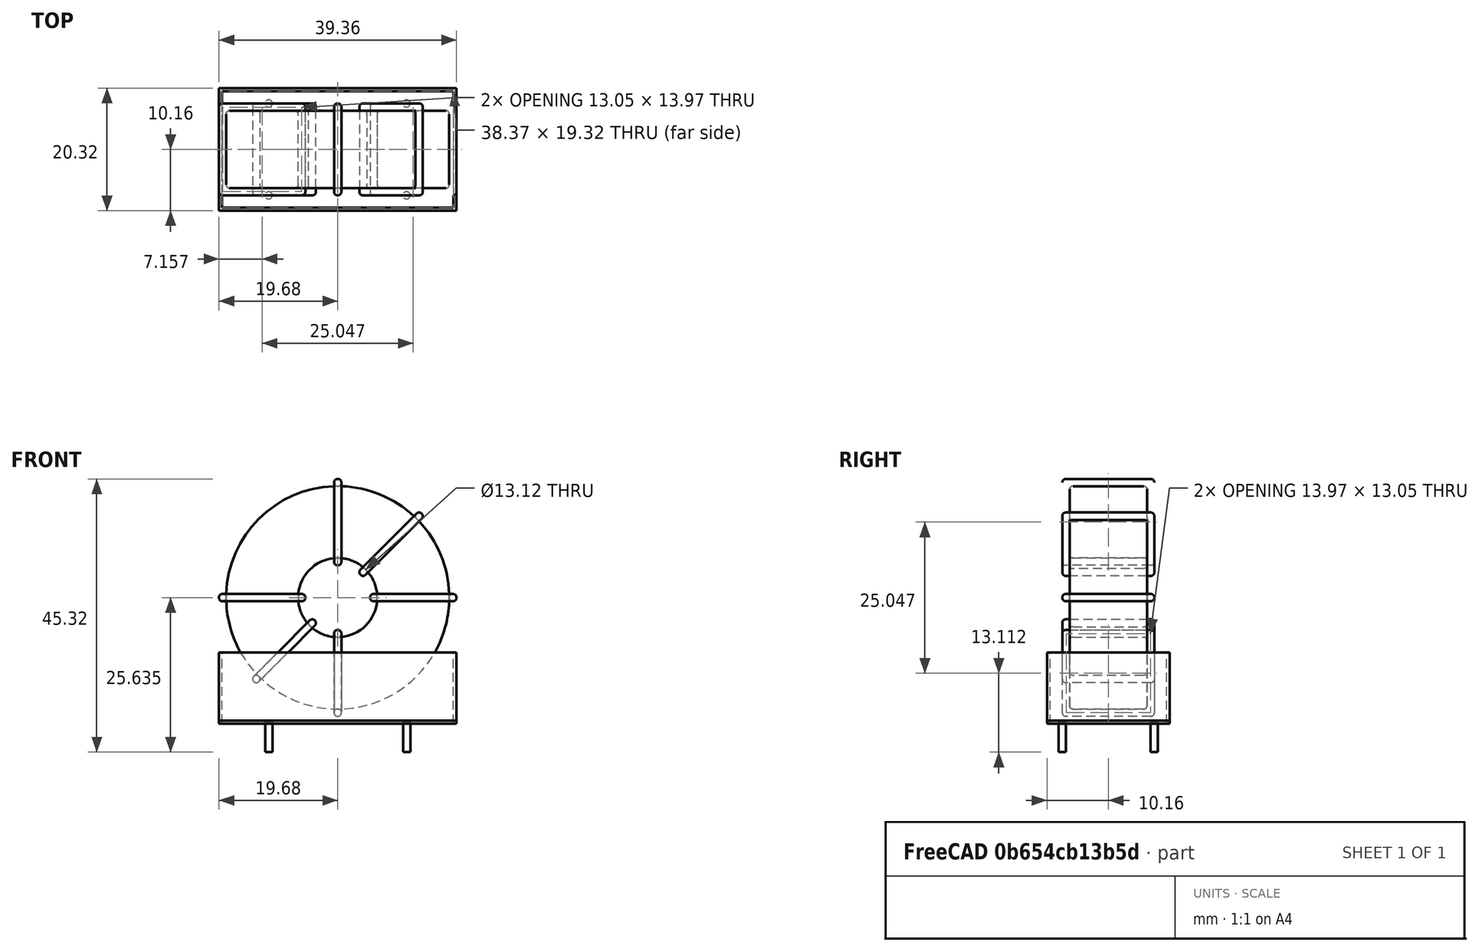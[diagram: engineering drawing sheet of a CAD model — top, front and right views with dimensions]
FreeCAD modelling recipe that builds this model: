
FCSTD DOCUMENT  (FreeCAD 0.16R6703 (Git))
Label: L_CommonModeChoke_Toroid_Vertical_L39.4mm_W20.3mm_Px15.24mm_Py22.86mm_Bourns_8100series
License: All rights reserved
LicenseURL: http://en.wikipedia.org/wiki/All_rights_reserved
objects: Sketcher::SketchObject×8, PartDesign::Pad×8, PartDesign::Fillet×5, Spreadsheet::Sheet×1
note: 29 computed .brp shape members not serialized (recipe doc carries the construction recipe); baked Part::Feature solids carry a one-line shape summary decoded from their .brp

FEATURE [Spreadsheet::Sheet] Spreadsheet  label="dimensions"
  cells = A1=Wx; B1(Wx)=39.37; C1(WW)=13.12333333333333; D1(iWx)=39.37; A2=Wy; B2(Wy)=15.24; D2(iWy)=20.32; A3=RM; B3(RMx)=15.24; C3(RMy)=22.86; A4=d_wire; B4(d_wire)=1.2; A5=H; B5(H)=31; A6=offsetx; B6(offsetx)=8.254999999999999
FEATURE [Sketcher::SketchObject] Sketch
  Placement = pos=(11.43,-7.62,0) rot=(1,0,0;1.5708rad)
  expr: Placement.Base.x = Spreadsheet.RMy / 2
  expr: Constraints[4] = Spreadsheet.WW / 2
  expr: Placement.Base.y = -Spreadsheet.RMx / 2
  expr: Constraints[0] = Spreadsheet.Wx / 2 - Spreadsheet.d_wire
  expr: Constraints[2] = Spreadsheet.Wx / 2 + Spreadsheet.d_wire + 0.5
  sketch-geometry (2):
    g0: Circle CenterX=0 CenterY=21.385 CenterZ=0 NormalX=0 NormalY=0 NormalZ=1 Radius=18.485
    g1: Circle CenterX=0 CenterY=21.385 CenterZ=0 NormalX=0 NormalY=0 NormalZ=1 Radius=6.56167
  constraints (5):
    c: Radius(g0) = 18.485
    c: DistanceX(g-1,g0) = 0
    c: DistanceY(g-1,g0) = 21.385
    c: Coincident(g1,g0)
    c: Radius(g1) = 6.56167
FEATURE [PartDesign::Pad] Pad
  Length = 12.84
  Length2 = 100
  Midplane = true
  Placement = pos=(11.43,-7.62,0) rot=(1,0,0;1.5708rad)
  Sketch = -> Sketch
  Type = 0
  expr: Length = Spreadsheet.Wy - 2 * Spreadsheet.d_wire
FEATURE [Sketcher::SketchObject] Sketch001
  Placement = pos=(0,0,0.75) rot=(0,0,1;0rad)
  expr: Constraints[4] = Spreadsheet.RMy
  expr: Constraints[2] = -Spreadsheet.RMx
  expr: Constraints[1] = Spreadsheet.d_wire / 2
  sketch-geometry (4):
    g0: Circle CenterX=0 CenterY=0 CenterZ=0 NormalX=0 NormalY=0 NormalZ=1 Radius=0.6
    g1: Circle CenterX=22.86 CenterY=-15.24 CenterZ=0 NormalX=0 NormalY=0 NormalZ=1 Radius=0.6
    g2: Circle CenterX=0 CenterY=-15.24 CenterZ=0 NormalX=0 NormalY=0 NormalZ=1 Radius=0.6
    g3: Circle CenterX=22.86 CenterY=0 CenterZ=0 NormalX=0 NormalY=0 NormalZ=1 Radius=0.6
  constraints (11):
    c: Equal(g0,g1)
    c: Radius(g0) = 0.6
    c: DistanceY(g-1,g1) = -15.24
    c: Coincident(g0,g-1)
    c: DistanceX(g-1,g1) = 22.86
    c: PointOnObject(g2,g-2)
    c: DistanceY(g-1,g3) = 0
    c: DistanceY(g2,g1) = 0
    c: DistanceX(g3,g1) = 0
    c: Equal(g3,g2)
    c: Equal(g2,g1)
FEATURE [PartDesign::Pad] Pad001
  Length = 5
  Length2 = 0
  Placement = pos=(0,0,0.75) rot=(0,0,1;0rad)
  Reversed = true
  Sketch = -> Sketch001
  Type = 0
FEATURE [PartDesign::Fillet] Fillet
  Base = -> Pad [Edge6,Edge3,Edge2]
  Placement = pos=(11.43,-7.62,0) rot=(1,0,0;1.5708rad)
  Radius = 0.5
FEATURE [Sketcher::SketchObject] Sketch003
  Placement = pos=(11.43,0,21.385) rot=(1,0,0;3.14159rad)
  expr: Placement.Base.x = Spreadsheet.RMy / 2
  expr: Constraints[18] = Spreadsheet.d_wire
  expr: Constraints[16] = Spreadsheet.d_wire
  expr: Constraints[19] = Spreadsheet.d_wire
  expr: Constraints[17] = Spreadsheet.d_wire
  expr: Placement.Base.y = -1 * (Spreadsheet.RMx - Spreadsheet.Wy) / 2
  expr: Constraints[21] = (Spreadsheet.Wx - Spreadsheet.WW) / 2 - Spreadsheet.d_wire
  expr: Constraints[22] = Spreadsheet.Wx / 2 - Spreadsheet.d_wire
  expr: Constraints[43] = Spreadsheet.d_wire
  expr: Constraints[48] = Spreadsheet.Wx - Spreadsheet.d_wire * 2
  expr: Constraints[49] = Spreadsheet.Wy
  expr: Placement.Base.z = Spreadsheet.Wx / 2 + Spreadsheet.d_wire + 0.5
  sketch-geometry (16):
    g0: LineSegment StartX=-5.36167 StartY=0 StartZ=0 EndX=-19.685 EndY=0 EndZ=0
    g1: LineSegment StartX=-19.685 StartY=0 StartZ=0 EndX=-19.685 EndY=15.24 EndZ=0
    g2: LineSegment StartX=-19.685 StartY=15.24 StartZ=0 EndX=-5.36167 EndY=15.24 EndZ=0
    g3: LineSegment StartX=-5.36167 StartY=15.24 StartZ=0 EndX=-5.36167 EndY=0 EndZ=0
    g4: LineSegment StartX=-18.485 StartY=14.04 StartZ=0 EndX=-6.56167 EndY=14.04 EndZ=0
    g5: LineSegment StartX=-6.56167 StartY=14.04 StartZ=0 EndX=-6.56167 EndY=1.2 EndZ=0
    g6: LineSegment StartX=-6.56167 StartY=1.2 StartZ=0 EndX=-18.485 EndY=1.2 EndZ=0
    g7: LineSegment StartX=-18.485 StartY=1.2 StartZ=0 EndX=-18.485 EndY=14.04 EndZ=0
    g8: LineSegment StartX=5.36167 StartY=15.24 StartZ=0 EndX=19.685 EndY=15.24 EndZ=0
    g9: LineSegment StartX=19.685 StartY=15.24 StartZ=0 EndX=19.685 EndY=0 EndZ=0
    g10: LineSegment StartX=19.685 StartY=0 StartZ=0 EndX=5.36167 EndY=0 EndZ=0
    g11: LineSegment StartX=5.36167 StartY=0 StartZ=0 EndX=5.36167 EndY=15.24 EndZ=0
    g12: LineSegment StartX=6.56167 StartY=14.04 StartZ=0 EndX=18.485 EndY=14.04 EndZ=0
    g13: LineSegment StartX=18.485 StartY=14.04 StartZ=0 EndX=18.485 EndY=1.2 EndZ=0
    g14: LineSegment StartX=18.485 StartY=1.2 StartZ=0 EndX=6.56167 EndY=1.2 EndZ=0
    g15: LineSegment StartX=6.56167 StartY=1.2 StartZ=0 EndX=6.56167 EndY=14.04 EndZ=0
  constraints (50):
    c: Horizontal(g0)
    c: Coincident(g1,g0)
    c: Vertical(g1)
    c: Coincident(g2,g1)
    c: Horizontal(g2)
    c: Coincident(g3,g2)
    c: Coincident(g3,g0)
    c: Vertical(g3)
    c: Coincident(g4,g5)
    c: Coincident(g5,g6)
    c: Coincident(g6,g7)
    c: Coincident(g7,g4)
    c: Horizontal(g4)
    c: Horizontal(g6)
    c: Vertical(g5)
    c: Vertical(g7)
    c: DistanceX(g1,g4) = 1.2
    c: DistanceY(g4,g1) = 1.2
    c: DistanceX(g5,g0) = 1.2
    c: DistanceY(g0,g5) = 1.2
    c: DistanceY(g-1,g0) = 0
    c: DistanceX(g6,g6) = 11.9233
    c: DistanceX(g6,g-1) = 18.485
    c: Coincident(g8,g9)
    c: Coincident(g9,g10)
    c: Coincident(g10,g11)
    c: Coincident(g11,g8)
    c: Horizontal(g8)
    c: Horizontal(g10)
    c: Vertical(g9)
    c: Vertical(g11)
    c: Coincident(g12,g13)
    c: Coincident(g13,g14)
    c: Coincident(g14,g15)
    c: Coincident(g15,g12)
    c: Horizontal(g12)
    c: Horizontal(g14)
    c: Vertical(g13)
    c: Vertical(g15)
    c: DistanceY(g8,g2) = 0
    c: DistanceY(g10,g0) = 0
    c: DistanceY(g14,g5) = 0
    c: DistanceY(g12,g4) = 0
    c: DistanceX(g8,g12) = 1.2
    c: Equal(g8,g2)
    c: Equal(g12,g4)
    c: Equal(g9,g1)
    c: Equal(g13,g7)
    c: DistanceX(g4,g12) = 36.97
    c: DistanceY(g0,g1) = 15.24
FEATURE [PartDesign::Pad] Pad002
  Length = 1.2
  Length2 = 100
  Midplane = true
  Placement = pos=(11.43,0,21.385) rot=(1,0,0;3.14159rad)
  Sketch = -> Sketch003
  Type = 0
  expr: Length = Spreadsheet.d_wire
FEATURE [PartDesign::Fillet] Fillet001
  Base = -> Pad002 [Edge38,Edge41,Edge42,Edge43,Edge29,Edge32,Edge33,Edge34,Edge25,Edge35,Edge36,Edge13,Edge14,Edge15,Edge16,Edge17,Edge18,Edge19,Edge1,Edge2,Edge3,Edge4,Edge5,Edge6,Edge7,Edge37,Edge39,Edge40,Edge20,Edge23,Edge24,Edge21,Edge22,Edge8,Edge9,Edge10,Edge11,Edge12,Edge26,Edge27,+8 more]
  Placement = pos=(11.43,0,21.385) rot=(1,0,0;3.14159rad)
  Radius = 0.564
  expr: Radius = Spreadsheet.d_wire * 0.47
FEATURE [Sketcher::SketchObject] Sketch004
  Placement = pos=(11.43,0,21.385) rot=(0.92388,0,0.382683;3.14159rad)
  expr: Placement.Base.x = Spreadsheet.RMy / 2
  expr: Constraints[18] = Spreadsheet.d_wire
  expr: Constraints[16] = Spreadsheet.d_wire
  expr: Constraints[19] = Spreadsheet.d_wire
  expr: Constraints[17] = Spreadsheet.d_wire
  expr: Placement.Base.y = -1 * (Spreadsheet.RMx - Spreadsheet.Wy) / 2
  expr: Constraints[21] = (Spreadsheet.Wx - Spreadsheet.WW) / 2 - Spreadsheet.d_wire
  expr: Constraints[22] = Spreadsheet.Wx / 2 - Spreadsheet.d_wire
  expr: Constraints[43] = Spreadsheet.d_wire
  expr: Constraints[48] = Spreadsheet.Wx - 2 * Spreadsheet.d_wire
  expr: Constraints[49] = Spreadsheet.Wy
  expr: Placement.Base.z = Spreadsheet.Wx / 2 + Spreadsheet.d_wire + 0.5
  sketch-geometry (16):
    g0: LineSegment StartX=-5.36167 StartY=0 StartZ=0 EndX=-19.685 EndY=0 EndZ=0
    g1: LineSegment StartX=-19.685 StartY=0 StartZ=0 EndX=-19.685 EndY=15.24 EndZ=0
    g2: LineSegment StartX=-19.685 StartY=15.24 StartZ=0 EndX=-5.36167 EndY=15.24 EndZ=0
    g3: LineSegment StartX=-5.36167 StartY=15.24 StartZ=0 EndX=-5.36167 EndY=0 EndZ=0
    g4: LineSegment StartX=-18.485 StartY=14.04 StartZ=0 EndX=-6.56167 EndY=14.04 EndZ=0
    g5: LineSegment StartX=-6.56167 StartY=14.04 StartZ=0 EndX=-6.56167 EndY=1.2 EndZ=0
    g6: LineSegment StartX=-6.56167 StartY=1.2 StartZ=0 EndX=-18.485 EndY=1.2 EndZ=0
    g7: LineSegment StartX=-18.485 StartY=1.2 StartZ=0 EndX=-18.485 EndY=14.04 EndZ=0
    g8: LineSegment StartX=5.36167 StartY=15.24 StartZ=0 EndX=19.685 EndY=15.24 EndZ=0
    g9: LineSegment StartX=19.685 StartY=15.24 StartZ=0 EndX=19.685 EndY=0 EndZ=0
    g10: LineSegment StartX=19.685 StartY=0 StartZ=0 EndX=5.36167 EndY=0 EndZ=0
    g11: LineSegment StartX=5.36167 StartY=0 StartZ=0 EndX=5.36167 EndY=15.24 EndZ=0
    g12: LineSegment StartX=6.56167 StartY=14.04 StartZ=0 EndX=18.485 EndY=14.04 EndZ=0
    g13: LineSegment StartX=18.485 StartY=14.04 StartZ=0 EndX=18.485 EndY=1.2 EndZ=0
    g14: LineSegment StartX=18.485 StartY=1.2 StartZ=0 EndX=6.56167 EndY=1.2 EndZ=0
    g15: LineSegment StartX=6.56167 StartY=1.2 StartZ=0 EndX=6.56167 EndY=14.04 EndZ=0
  constraints (50):
    c: Horizontal(g0)
    c: Coincident(g1,g0)
    c: Vertical(g1)
    c: Coincident(g2,g1)
    c: Horizontal(g2)
    c: Coincident(g3,g2)
    c: Coincident(g3,g0)
    c: Vertical(g3)
    c: Coincident(g4,g5)
    c: Coincident(g5,g6)
    c: Coincident(g6,g7)
    c: Coincident(g7,g4)
    c: Horizontal(g4)
    c: Horizontal(g6)
    c: Vertical(g5)
    c: Vertical(g7)
    c: DistanceX(g1,g4) = 1.2
    c: DistanceY(g4,g1) = 1.2
    c: DistanceX(g5,g0) = 1.2
    c: DistanceY(g0,g5) = 1.2
    c: DistanceY(g-1,g0) = 0
    c: DistanceX(g6,g6) = 11.9233
    c: DistanceX(g6,g-1) = 18.485
    c: Coincident(g8,g9)
    c: Coincident(g9,g10)
    c: Coincident(g10,g11)
    c: Coincident(g11,g8)
    c: Horizontal(g8)
    c: Horizontal(g10)
    c: Vertical(g9)
    c: Vertical(g11)
    c: Coincident(g12,g13)
    c: Coincident(g13,g14)
    c: Coincident(g14,g15)
    c: Coincident(g15,g12)
    c: Horizontal(g12)
    c: Horizontal(g14)
    c: Vertical(g13)
    c: Vertical(g15)
    c: DistanceY(g8,g2) = 0
    c: DistanceY(g10,g0) = 0
    c: DistanceY(g14,g5) = 0
    c: DistanceY(g12,g4) = 0
    c: DistanceX(g8,g12) = 1.2
    c: Equal(g8,g2)
    c: Equal(g12,g4)
    c: Equal(g9,g1)
    c: Equal(g13,g7)
    c: DistanceX(g4,g12) = 36.97
    c: DistanceY(g0,g1) = 15.24
FEATURE [PartDesign::Pad] Pad003
  Length = 1.2
  Length2 = 100
  Midplane = true
  Placement = pos=(11.43,0,21.385) rot=(0.92388,0,0.382683;3.14159rad)
  Sketch = -> Sketch004
  Type = 0
  expr: Length = Spreadsheet.d_wire
FEATURE [PartDesign::Fillet] Fillet002
  Base = -> Pad003 [Edge38,Edge41,Edge42,Edge43,Edge29,Edge32,Edge33,Edge34,Edge25,Edge35,Edge36,Edge13,Edge14,Edge15,Edge16,Edge17,Edge18,Edge19,Edge1,Edge2,Edge3,Edge4,Edge5,Edge6,Edge7,Edge37,Edge39,Edge40,Edge20,Edge23,Edge24,Edge21,Edge22,Edge8,Edge9,Edge10,Edge11,Edge12,Edge26,Edge27,+8 more]
  Placement = pos=(11.43,0,21.385) rot=(0.92388,0,0.382683;3.14159rad)
  Radius = 0.564
  expr: Radius = Spreadsheet.d_wire * 0.47
FEATURE [Sketcher::SketchObject] Sketch005
  Placement = pos=(11.43,0,21.385) rot=(0.92388,0,-0.382683;3.14159rad)
  expr: Placement.Base.x = Spreadsheet.RMy / 2
  expr: Constraints[18] = Spreadsheet.d_wire
  expr: Constraints[16] = Spreadsheet.d_wire
  expr: Constraints[19] = Spreadsheet.d_wire
  expr: Constraints[17] = Spreadsheet.d_wire
  expr: Placement.Base.y = -1 * (Spreadsheet.RMx - Spreadsheet.Wy) / 2
  expr: Constraints[21] = (Spreadsheet.Wx - Spreadsheet.WW) / 2 - Spreadsheet.d_wire
  expr: Constraints[22] = Spreadsheet.Wx / 2 - Spreadsheet.d_wire
  expr: Constraints[43] = Spreadsheet.d_wire
  expr: Constraints[48] = Spreadsheet.Wx - 2 * Spreadsheet.d_wire
  expr: Constraints[49] = Spreadsheet.Wy
  expr: Placement.Base.z = Spreadsheet.Wx / 2 + Spreadsheet.d_wire + 0.5
  sketch-geometry (16):
    g0: LineSegment StartX=-5.36167 StartY=0 StartZ=0 EndX=-19.685 EndY=0 EndZ=0
    g1: LineSegment StartX=-19.685 StartY=0 StartZ=0 EndX=-19.685 EndY=15.24 EndZ=0
    g2: LineSegment StartX=-19.685 StartY=15.24 StartZ=0 EndX=-5.36167 EndY=15.24 EndZ=0
    g3: LineSegment StartX=-5.36167 StartY=15.24 StartZ=0 EndX=-5.36167 EndY=0 EndZ=0
    g4: LineSegment StartX=-18.485 StartY=14.04 StartZ=0 EndX=-6.56167 EndY=14.04 EndZ=0
    g5: LineSegment StartX=-6.56167 StartY=14.04 StartZ=0 EndX=-6.56167 EndY=1.2 EndZ=0
    g6: LineSegment StartX=-6.56167 StartY=1.2 StartZ=0 EndX=-18.485 EndY=1.2 EndZ=0
    g7: LineSegment StartX=-18.485 StartY=1.2 StartZ=0 EndX=-18.485 EndY=14.04 EndZ=0
    g8: LineSegment StartX=5.36167 StartY=15.24 StartZ=0 EndX=19.685 EndY=15.24 EndZ=0
    g9: LineSegment StartX=19.685 StartY=15.24 StartZ=0 EndX=19.685 EndY=0 EndZ=0
    g10: LineSegment StartX=19.685 StartY=0 StartZ=0 EndX=5.36167 EndY=0 EndZ=0
    g11: LineSegment StartX=5.36167 StartY=0 StartZ=0 EndX=5.36167 EndY=15.24 EndZ=0
    g12: LineSegment StartX=6.56167 StartY=14.04 StartZ=0 EndX=18.485 EndY=14.04 EndZ=0
    g13: LineSegment StartX=18.485 StartY=14.04 StartZ=0 EndX=18.485 EndY=1.2 EndZ=0
    g14: LineSegment StartX=18.485 StartY=1.2 StartZ=0 EndX=6.56167 EndY=1.2 EndZ=0
    g15: LineSegment StartX=6.56167 StartY=1.2 StartZ=0 EndX=6.56167 EndY=14.04 EndZ=0
  constraints (50):
    c: Horizontal(g0)
    c: Coincident(g1,g0)
    c: Vertical(g1)
    c: Coincident(g2,g1)
    c: Horizontal(g2)
    c: Coincident(g3,g2)
    c: Coincident(g3,g0)
    c: Vertical(g3)
    c: Coincident(g4,g5)
    c: Coincident(g5,g6)
    c: Coincident(g6,g7)
    c: Coincident(g7,g4)
    c: Horizontal(g4)
    c: Horizontal(g6)
    c: Vertical(g5)
    c: Vertical(g7)
    c: DistanceX(g1,g4) = 1.2
    c: DistanceY(g4,g1) = 1.2
    c: DistanceX(g5,g0) = 1.2
    c: DistanceY(g0,g5) = 1.2
    c: DistanceY(g-1,g0) = 0
    c: DistanceX(g6,g6) = 11.9233
    c: DistanceX(g6,g-1) = 18.485
    c: Coincident(g8,g9)
    c: Coincident(g9,g10)
    c: Coincident(g10,g11)
    c: Coincident(g11,g8)
    c: Horizontal(g8)
    c: Horizontal(g10)
    c: Vertical(g9)
    c: Vertical(g11)
    c: Coincident(g12,g13)
    c: Coincident(g13,g14)
    c: Coincident(g14,g15)
    c: Coincident(g15,g12)
    c: Horizontal(g12)
    c: Horizontal(g14)
    c: Vertical(g13)
    c: Vertical(g15)
    c: DistanceY(g8,g2) = 0
    c: DistanceY(g10,g0) = 0
    c: DistanceY(g14,g5) = 0
    c: DistanceY(g12,g4) = 0
    c: DistanceX(g8,g12) = 1.2
    c: Equal(g8,g2)
    c: Equal(g12,g4)
    c: Equal(g9,g1)
    c: Equal(g13,g7)
    c: DistanceX(g4,g12) = 36.97
    c: DistanceY(g0,g1) = 15.24
FEATURE [PartDesign::Pad] Pad004
  Length = 1.2
  Length2 = 100
  Midplane = true
  Placement = pos=(11.43,0,21.385) rot=(0.92388,0,-0.382683;3.14159rad)
  Sketch = -> Sketch005
  Type = 0
  expr: Length = Spreadsheet.d_wire
FEATURE [PartDesign::Fillet] Fillet003
  Base = -> Pad004 [Edge38,Edge41,Edge42,Edge43,Edge29,Edge32,Edge33,Edge34,Edge25,Edge35,Edge36,Edge13,Edge14,Edge15,Edge16,Edge17,Edge18,Edge19,Edge1,Edge2,Edge3,Edge4,Edge5,Edge6,Edge7,Edge37,Edge39,Edge40,Edge20,Edge23,Edge24,Edge21,Edge22,Edge8,Edge9,Edge10,Edge11,Edge12,Edge26,Edge27,+8 more]
  Placement = pos=(11.43,0,21.385) rot=(0.92388,0,-0.382683;3.14159rad)
  Radius = 0.564
  expr: Radius = Spreadsheet.d_wire * 0.47
FEATURE [Sketcher::SketchObject] Sketch006
  Placement = pos=(11.43,0,21.385) rot=(0.707107,0,0.707107;3.14159rad)
  expr: Placement.Base.x = Spreadsheet.RMy / 2
  expr: Constraints[18] = Spreadsheet.d_wire
  expr: Constraints[16] = Spreadsheet.d_wire
  expr: Constraints[19] = Spreadsheet.d_wire
  expr: Constraints[17] = Spreadsheet.d_wire
  expr: Placement.Base.y = -1 * (Spreadsheet.RMx - Spreadsheet.Wy) / 2
  expr: Constraints[21] = (Spreadsheet.Wx - Spreadsheet.WW) / 2 - Spreadsheet.d_wire
  expr: Constraints[22] = Spreadsheet.Wx / 2 - Spreadsheet.d_wire
  expr: Constraints[43] = Spreadsheet.d_wire
  expr: Constraints[48] = Spreadsheet.Wx - Spreadsheet.d_wire * 2
  expr: Constraints[49] = Spreadsheet.Wy
  expr: Placement.Base.z = Spreadsheet.Wx / 2 + Spreadsheet.d_wire + 0.5
  sketch-geometry (16):
    g0: LineSegment StartX=-5.36167 StartY=0 StartZ=0 EndX=-19.685 EndY=0 EndZ=0
    g1: LineSegment StartX=-19.685 StartY=0 StartZ=0 EndX=-19.685 EndY=15.24 EndZ=0
    g2: LineSegment StartX=-19.685 StartY=15.24 StartZ=0 EndX=-5.36167 EndY=15.24 EndZ=0
    g3: LineSegment StartX=-5.36167 StartY=15.24 StartZ=0 EndX=-5.36167 EndY=0 EndZ=0
    g4: LineSegment StartX=-18.485 StartY=14.04 StartZ=0 EndX=-6.56167 EndY=14.04 EndZ=0
    g5: LineSegment StartX=-6.56167 StartY=14.04 StartZ=0 EndX=-6.56167 EndY=1.2 EndZ=0
    g6: LineSegment StartX=-6.56167 StartY=1.2 StartZ=0 EndX=-18.485 EndY=1.2 EndZ=0
    g7: LineSegment StartX=-18.485 StartY=1.2 StartZ=0 EndX=-18.485 EndY=14.04 EndZ=0
    g8: LineSegment StartX=5.36167 StartY=15.24 StartZ=0 EndX=19.685 EndY=15.24 EndZ=0
    g9: LineSegment StartX=19.685 StartY=15.24 StartZ=0 EndX=19.685 EndY=0 EndZ=0
    g10: LineSegment StartX=19.685 StartY=0 StartZ=0 EndX=5.36167 EndY=0 EndZ=0
    g11: LineSegment StartX=5.36167 StartY=0 StartZ=0 EndX=5.36167 EndY=15.24 EndZ=0
    g12: LineSegment StartX=6.56167 StartY=14.04 StartZ=0 EndX=18.485 EndY=14.04 EndZ=0
    g13: LineSegment StartX=18.485 StartY=14.04 StartZ=0 EndX=18.485 EndY=1.2 EndZ=0
    g14: LineSegment StartX=18.485 StartY=1.2 StartZ=0 EndX=6.56167 EndY=1.2 EndZ=0
    g15: LineSegment StartX=6.56167 StartY=1.2 StartZ=0 EndX=6.56167 EndY=14.04 EndZ=0
  constraints (50):
    c: Horizontal(g0)
    c: Coincident(g1,g0)
    c: Vertical(g1)
    c: Coincident(g2,g1)
    c: Horizontal(g2)
    c: Coincident(g3,g2)
    c: Coincident(g3,g0)
    c: Vertical(g3)
    c: Coincident(g4,g5)
    c: Coincident(g5,g6)
    c: Coincident(g6,g7)
    c: Coincident(g7,g4)
    c: Horizontal(g4)
    c: Horizontal(g6)
    c: Vertical(g5)
    c: Vertical(g7)
    c: DistanceX(g1,g4) = 1.2
    c: DistanceY(g4,g1) = 1.2
    c: DistanceX(g5,g0) = 1.2
    c: DistanceY(g0,g5) = 1.2
    c: DistanceY(g-1,g0) = 0
    c: DistanceX(g6,g6) = 11.9233
    c: DistanceX(g6,g-1) = 18.485
    c: Coincident(g8,g9)
    c: Coincident(g9,g10)
    c: Coincident(g10,g11)
    c: Coincident(g11,g8)
    c: Horizontal(g8)
    c: Horizontal(g10)
    c: Vertical(g9)
    c: Vertical(g11)
    c: Coincident(g12,g13)
    c: Coincident(g13,g14)
    c: Coincident(g14,g15)
    c: Coincident(g15,g12)
    c: Horizontal(g12)
    c: Horizontal(g14)
    c: Vertical(g13)
    c: Vertical(g15)
    c: DistanceY(g8,g2) = 0
    c: DistanceY(g10,g0) = 0
    c: DistanceY(g14,g5) = 0
    c: DistanceY(g12,g4) = 0
    c: DistanceX(g8,g12) = 1.2
    c: Equal(g8,g2)
    c: Equal(g12,g4)
    c: Equal(g9,g1)
    c: Equal(g13,g7)
    c: DistanceX(g4,g12) = 36.97
    c: DistanceY(g0,g1) = 15.24
FEATURE [PartDesign::Pad] Pad005
  Length = 1.2
  Length2 = 100
  Midplane = true
  Placement = pos=(11.43,0,21.385) rot=(0.707107,0,0.707107;3.14159rad)
  Sketch = -> Sketch006
  Type = 0
  expr: Length = Spreadsheet.d_wire
FEATURE [PartDesign::Fillet] Fillet004
  Base = -> Pad005 [Edge38,Edge41,Edge42,Edge43,Edge29,Edge32,Edge33,Edge34,Edge25,Edge35,Edge36,Edge13,Edge14,Edge15,Edge16,Edge17,Edge18,Edge19,Edge1,Edge2,Edge3,Edge4,Edge5,Edge6,Edge7,Edge37,Edge39,Edge40,Edge20,Edge23,Edge24,Edge21,Edge22,Edge8,Edge9,Edge10,Edge11,Edge12,Edge26,Edge27,+8 more]
  Placement = pos=(11.43,0,21.385) rot=(0.707107,0,0.707107;3.14159rad)
  Radius = 0.564
  expr: Radius = Spreadsheet.d_wire * 0.47
FEATURE [Sketcher::SketchObject] Sketch007
  Placement = pos=(11.43,0,0.5) rot=(0,0,1;0rad)
  expr: Placement.Base.x = Spreadsheet.RMy / 2
  expr: Placement.Base.z = 0.5
  expr: Constraints[11] = Spreadsheet.iWx / 2
  expr: Constraints[10] = (Spreadsheet.iWy - Spreadsheet.RMx) / 2
  expr: Constraints[9] = Spreadsheet.iWy
  expr: Constraints[8] = Spreadsheet.iWx
  sketch-geometry (4):
    g0: LineSegment StartX=-19.685 StartY=2.54 StartZ=0 EndX=19.685 EndY=2.54 EndZ=0
    g1: LineSegment StartX=19.685 StartY=2.54 StartZ=0 EndX=19.685 EndY=-17.78 EndZ=0
    g2: LineSegment StartX=19.685 StartY=-17.78 StartZ=0 EndX=-19.685 EndY=-17.78 EndZ=0
    g3: LineSegment StartX=-19.685 StartY=-17.78 StartZ=0 EndX=-19.685 EndY=2.54 EndZ=0
  constraints (12):
    c: Coincident(g0,g1)
    c: Coincident(g1,g2)
    c: Coincident(g2,g3)
    c: Coincident(g3,g0)
    c: Horizontal(g0)
    c: Horizontal(g2)
    c: Vertical(g1)
    c: Vertical(g3)
    c: DistanceX(g0,g0) = 39.37
    c: DistanceY(g3,g3) = 20.32
    c: DistanceY(g-1,g0) = 2.54
    c: DistanceX(g0,g-1) = 19.685
FEATURE [PartDesign::Pad] Pad006
  Length = 0.5
  Length2 = 100
  Placement = pos=(11.43,0,0.5) rot=(0,0,1;0rad)
  Sketch = -> Sketch007
  Type = 0
FEATURE [Sketcher::SketchObject] Sketch008
  Placement = pos=(11.43,0,0.5) rot=(0,0,1;0rad)
  expr: Placement.Base.x = Spreadsheet.RMy / 2
  expr: Constraints[8] = Spreadsheet.iWx
  expr: Constraints[9] = Spreadsheet.iWy
  expr: Constraints[10] = (Spreadsheet.iWy - Spreadsheet.RMx) / 2
  expr: Placement.Base.z = 0.5
  expr: Constraints[21] = 0.5
  expr: Constraints[11] = Spreadsheet.iWx / 2
  sketch-geometry (8):
    g0: LineSegment StartX=-19.685 StartY=2.54 StartZ=0 EndX=19.685 EndY=2.54 EndZ=0
    g1: LineSegment StartX=19.685 StartY=2.54 StartZ=0 EndX=19.685 EndY=-17.78 EndZ=0
    g2: LineSegment StartX=19.685 StartY=-17.78 StartZ=0 EndX=-19.685 EndY=-17.78 EndZ=0
    g3: LineSegment StartX=-19.685 StartY=-17.78 StartZ=0 EndX=-19.685 EndY=2.54 EndZ=0
    g4: LineSegment StartX=-19.185 StartY=2.04 StartZ=0 EndX=19.185 EndY=2.04 EndZ=0
    g5: LineSegment StartX=19.185 StartY=2.04 StartZ=0 EndX=19.185 EndY=-17.28 EndZ=0
    g6: LineSegment StartX=19.185 StartY=-17.28 StartZ=0 EndX=-19.185 EndY=-17.28 EndZ=0
    g7: LineSegment StartX=-19.185 StartY=-17.28 StartZ=0 EndX=-19.185 EndY=2.04 EndZ=0
  constraints (24):
    c: Coincident(g0,g1)
    c: Coincident(g1,g2)
    c: Coincident(g2,g3)
    c: Coincident(g3,g0)
    c: Horizontal(g0)
    c: Horizontal(g2)
    c: Vertical(g1)
    c: Vertical(g3)
    c: DistanceX(g0,g0) = 39.37
    c: DistanceY(g3,g3) = 20.32
    c: DistanceY(g-1,g0) = 2.54
    c: DistanceX(g0,g-1) = 19.685
    c: Coincident(g4,g5)
    c: Coincident(g5,g6)
    c: Coincident(g6,g7)
    c: Coincident(g7,g4)
    c: Horizontal(g4)
    c: Horizontal(g6)
    c: Vertical(g5)
    c: Vertical(g7)
    c: DistanceX(g5,g1) = 0.5
    c: DistanceY(g1,g5) = 0.5
    c: DistanceX(g0,g4) = 0.5
    c: DistanceY(g4,g0) = 0.5
FEATURE [PartDesign::Pad] Pad007
  Length = 11.811
  Length2 = 100
  Placement = pos=(11.43,0,0.5) rot=(0,0,1;0rad)
  Sketch = -> Sketch008
  Type = 0
  expr: Length = Spreadsheet.Wx * 0.3
